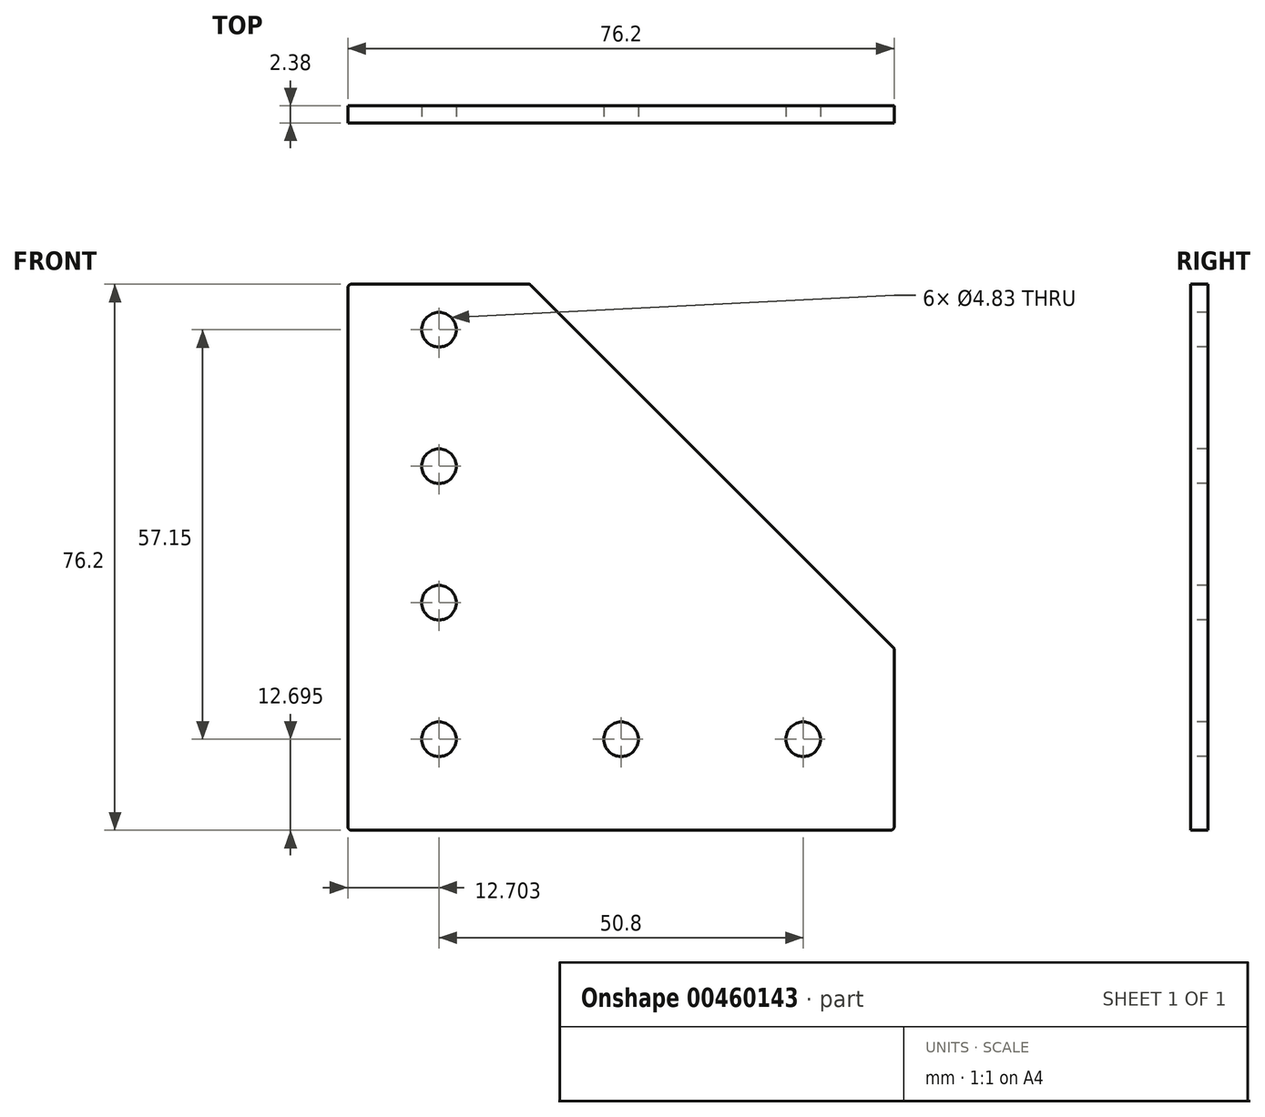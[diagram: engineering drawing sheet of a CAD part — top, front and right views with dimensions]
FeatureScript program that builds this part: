
annotation { "Feature Type Name" : "Feature", "Feature Type Description" : "" }
export const myFeature = defineFeature(function(context is Context, id is Id, definition is map)
    precondition{}
    {
        {
            var Q0;
            Q0=qCreatedBy(makeId("Front.planeOp"),FACE);
            var sketch = newSketch(context, id + "F0", { "sketchPlane" : qUnion([Q0])});
            skLineSegment(sketch, "E0", {"start": v(-34.22, 37.99) * mm, "end": v(-34.22, -38.21) * mm});
            skLineSegment(sketch, "E1", {"start": v(-34.22, -38.21) * mm, "end": v(41.98, -38.21) * mm});
            skLineSegment(sketch, "E2", {"start": v(41.98, -38.21) * mm, "end": v(41.98, -12.81) * mm});
            skLineSegment(sketch, "E3", {"start": v(-34.22, 37.99) * mm, "end": v(-8.82, 37.99) * mm});
            skLineSegment(sketch, "E4", {"start": v(-8.82, 37.99) * mm, "end": v(41.98, -12.81) * mm});
            skLineSegment(sketch, "E5", {"start": v(-8.82, 37.99) * mm, "end": v(-8.82, -38.21) * mm, "construction": true});
            skLineSegment(sketch, "E6", {"start": v(41.98, -12.81) * mm, "end": v(-34.22, -12.81) * mm, "construction": true});
            skSolve(sketch);
        }
        {
            var Q0;
            Q0=makeQuery(id+"F0.imprint","IMPRINT",FACE,{"disambiguationData":[TD([[makeQuery(id+"F0.imprint","IMPRINT",EDGE,{"derivedFrom":sQuery(id+"F0.wireOp",EDGE,"E0")}),1.0]])]});
            extrude(context, id + "F1", {"entities" : qUnion([Q0]), "depth" : 2.38 * mm});
        }
        {
            var Q0;
            Q0=makeQuery(id+"F1.opExtrude","SWEPT_EDGE",EDGE,{"disambiguationData":[OSD([sQuery(id+"F0.wireOp",EDGE,"E0"),sQuery(id+"F0.wireOp",EDGE,"E3")])]});
            var Q1;
            Q1=makeQuery(id+"F1.opExtrude","SWEPT_EDGE",EDGE,{"disambiguationData":[OSD([sQuery(id+"F0.wireOp",EDGE,"E3"),sQuery(id+"F0.wireOp",EDGE,"E4")])]});
            var Q2;
            Q2=makeQuery(id+"F1.opExtrude","SWEPT_EDGE",EDGE,{"disambiguationData":[OSD([sQuery(id+"F0.wireOp",EDGE,"E0"),sQuery(id+"F0.wireOp",EDGE,"E1")])]});
            var Q3;
            Q3=makeQuery(id+"F1.opExtrude","SWEPT_EDGE",EDGE,{"disambiguationData":[OSD([sQuery(id+"F0.wireOp",EDGE,"E2"),sQuery(id+"F0.wireOp",EDGE,"E4")])]});
            var Q4;
            Q4=makeQuery(id+"F1.opExtrude","SWEPT_EDGE",EDGE,{"disambiguationData":[OSD([sQuery(id+"F0.wireOp",EDGE,"E1"),sQuery(id+"F0.wireOp",EDGE,"E2")])]});
            fillet(context, id + "F2", {"entities" : qUnion([Q0, Q1, Q2, Q3, Q4]), "radius" : 0.5 * mm, "tangentPropagation" : true, "allowEdgeOverflow" : false});
        }
        {
            var Q0;
            Q0=makeQuery(id+"F1.opExtrude","CAP_FACE",FACE,{"disambiguationData":[OSD([sQuery(id+"F0.wireOp",EDGE,"E0"),sQuery(id+"F0.wireOp",EDGE,"E1"),sQuery(id+"F0.wireOp",EDGE,"E2"),sQuery(id+"F0.wireOp",EDGE,"E3"),sQuery(id+"F0.wireOp",EDGE,"E4")])],"isStart":false});
            var sketch = newSketch(context, id + "F3", { "sketchPlane" : qUnion([Q0])});
            skCircle(sketch, "E7", {"center": v(-21.52, 31.64) * mm, "radius": 2.41 * mm});
            skCircle(sketch, "E8", {"center": v(29.28, -25.51) * mm, "radius": 2.41 * mm});
            skCircle(sketch, "E9", {"center": v(3.88, -25.51) * mm, "radius": 2.41 * mm});
            skCircle(sketch, "E10", {"center": v(-21.52, -25.51) * mm, "radius": 2.41 * mm});
            skCircle(sketch, "E11", {"center": v(-21.52, 12.59) * mm, "radius": 2.41 * mm});
            skCircle(sketch, "E12", {"center": v(-21.52, -6.46) * mm, "radius": 2.41 * mm});
            skSolve(sketch);
        }
        {
            var Q0;
            Q0=makeQuery(id+"F3.imprint","IMPRINT",FACE,{"disambiguationData":[TD([[makeQuery(id+"F3.imprint","IMPRINT",EDGE,{"derivedFrom":sQuery(id+"F3.wireOp",EDGE,"E7")}),1.0]])]});
            var Q1;
            Q1=makeQuery(id+"F3.imprint","IMPRINT",FACE,{"disambiguationData":[TD([[makeQuery(id+"F3.imprint","IMPRINT",EDGE,{"derivedFrom":sQuery(id+"F3.wireOp",EDGE,"E11")}),1.0]])]});
            var Q2;
            Q2=makeQuery(id+"F3.imprint","IMPRINT",FACE,{"disambiguationData":[TD([[makeQuery(id+"F3.imprint","IMPRINT",EDGE,{"derivedFrom":sQuery(id+"F3.wireOp",EDGE,"E12")}),1.0]])]});
            var Q3;
            Q3=makeQuery(id+"F3.imprint","IMPRINT",FACE,{"disambiguationData":[TD([[makeQuery(id+"F3.imprint","IMPRINT",EDGE,{"derivedFrom":sQuery(id+"F3.wireOp",EDGE,"E10")}),1.0]])]});
            var Q4;
            Q4=makeQuery(id+"F3.imprint","IMPRINT",FACE,{"disambiguationData":[TD([[makeQuery(id+"F3.imprint","IMPRINT",EDGE,{"derivedFrom":sQuery(id+"F3.wireOp",EDGE,"E9")}),1.0]])]});
            var Q5;
            Q5=makeQuery(id+"F3.imprint","IMPRINT",FACE,{"disambiguationData":[TD([[makeQuery(id+"F3.imprint","IMPRINT",EDGE,{"derivedFrom":sQuery(id+"F3.wireOp",EDGE,"E8")}),1.0]])]});
            extrude(context, id + "F4", {"entities" : qUnion([Q0, Q1, Q2, Q3, Q4, Q5]), "operationType" : NewBodyOperationType.REMOVE, "oppositeDirection" : true, "depth" : 2.38 * mm});
        }
    });
